# Revit family: Facet II - Generic
name_source: partatom
category: Lighting Fixtures
revit_build: Autodesk Revit Architecture 2014 (Build: 20130308_1515(x64)
units: mm (PartAtom-declared; Revit-internal decimal feet)

## types (3) — shared parameters
ArticleNumber = See URL hyperlink
AssetType = Moveable/Fixed
BSAB 96 = SNB.2
BallastsCELMAEnergyEfficiencyIndex = Class A1/A2
CCSClassCode = UAC
CCSClassName = Belysningsarmatur
CCSTopnode = L
Cassette Depth = 0 mm
Cassette Width = 560 mm
Color Filter = 16777215
Colour = White
ControlGearPosition = Integrated
Description = 70-80-35 General Lighting Systems
Dimming Lamp Color Temperature Shift = <None>
DocumentReference = See URL hyperlink
Documentation = See URL hyperlink
Finish = Powder coated
Frame = Riegens_Steel_Powder coated white RAL901025
Frame Depth = 112 mm
Glass = Riegens_Glass_opal
HasProtectiveEarth = TRUE
Height 1 = 80 mm
IP_Code = IP20
IfcExportAs = IfcLightFixtureType
IfcExportType = NOTDEFINED
InsulationStandardClass = Class 1
InternalFuse = Only required in emergency versions
LampColourRenderingIndex = Ra>80
LampType = LED
LightFixtureMountingType = Suspended
LightFixturePlacingType = Ceiling
LightSource = LED 3000K / 4000K
LuminairePowerFactor = >0,9
Manufacturer = Riegens A/S
ManufacturerURL = www.riegens.com
Material = Steel, Lens optic from PMMA and PC.
NominalVoltage = 220-240V
Optic = Direct: Prismatic optic, Indirect: Clear PC.
PhaseReference = IEC recommendations
PhotometricPerformance = In accordance with BS EN 13032-1
ProductInformation = http://riegens.com
Shape = Rectangle
Tilt Angle = 90.00°
Uniclass 1.4 = JY73
Uniclass2 = Pr_70_70_49_43 Light-Emitting Diode (LED) Luminaires
Version = v.1.0

## per-type parameters (varying)
| type | BIMObjectName | Fixing point Suspended | Frame Width | Glass Depth | Glass Width | LampRating | LuminaireType | Photometric Web File | Size | Suspended Distance | TotalWattage | Void | Void Thickness |
| Facet II 1200 Asymmetric | Facet II 1200 Asymmetric.rfa | 1000 mm | 1196 mm | 65 mm | 1108 mm | 21W | Direct Asymmetric LED Luminaire | Facet II 1200 DA 21W 4000K.ies | 112 x 1196 x 80 mm | 420 mm | Max. 23W | No | 5 mm |
| Facet II 1700 DI | Facet II 1700 DI.rfa | 1600 mm | 1756 mm | 100 mm | 1700 mm | 56W | Direct/Indirect LED Luminaire | Facet II 1700 DI 56W 4000K Lens C.ies | 112 x 1756 x 80 mm | 250 mm | Max. 58W | Yes | -5 mm |
| Facet II 1200 DI | Facet II 1200 DI.rfa | 1000 mm | 1196 mm | 100 mm | 1140 mm | 25W / 35W | Direct/Indirect LED Luminaire | Facet II 1200 DI 25W 4000K Lens C.ies | 112 x 1196 x 80 mm | 420 mm | Max. 27W / 37W | Yes | -5 mm |

note: column(s) folded — value = type name in every type: ModelReference

## geometry (parser evidence)
native form markers: Blend x82, Sweep x1
no freeform markers — native parametric forms only
